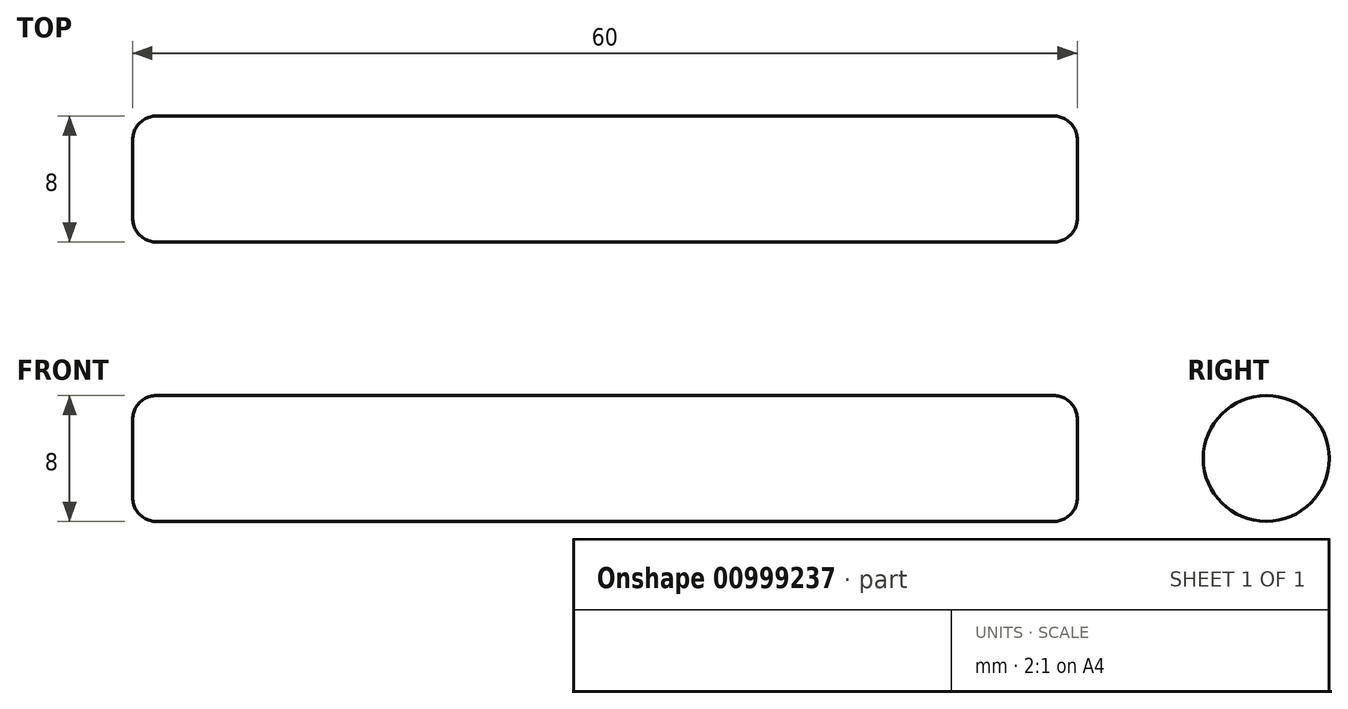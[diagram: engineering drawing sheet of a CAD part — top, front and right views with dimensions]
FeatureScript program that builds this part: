
annotation { "Feature Type Name" : "Feature", "Feature Type Description" : "" }
export const myFeature = defineFeature(function(context is Context, id is Id, definition is map)
    precondition{}
    {
        {
            var Q0;
            Q0=qCreatedBy(makeId("Front.planeOp"),FACE);
            var sketch = newSketch(context, id + "F0", { "sketchPlane" : qUnion([Q0])});
            skLineSegment(sketch, "E0", {"start": v(-30, 0) * mm, "end": v(30, 0) * mm});
            skLineSegment(sketch, "E1", {"start": v(30, 0) * mm, "end": v(30, 2.5) * mm});
            skLineSegment(sketch, "E2", {"start": v(-30, 0) * mm, "end": v(-30, 2.5) * mm});
            skArc(sketch, "E3", {"start": v(-30, 2.5) * mm, "mid": v(-29.56, 3.56) * mm, "end": v(-28.5, 4) * mm});
            skArc(sketch, "E4", {"start": v(30, 2.5) * mm, "mid": v(29.56, 3.56) * mm, "end": v(28.5, 4) * mm});
            skLineSegment(sketch, "E5", {"start": v(-28.5, 4) * mm, "end": v(28.5, 4) * mm});
            skSolve(sketch);
        }
        {
            var Q0;
            Q0=qSketchRegion(id+"F0",true);
            var Q1;
            Q1=sQuery(id+"F0.wireOp",EDGE,"E0");
            revolve(context, id + "F1", {"surfaceOperationType" : NewSurfaceOperationType.NEW, "entities" : qUnion([Q0]), "axis" : qUnion([Q1]), "revolveType" : RevolveType.FULL});
        }
    });
